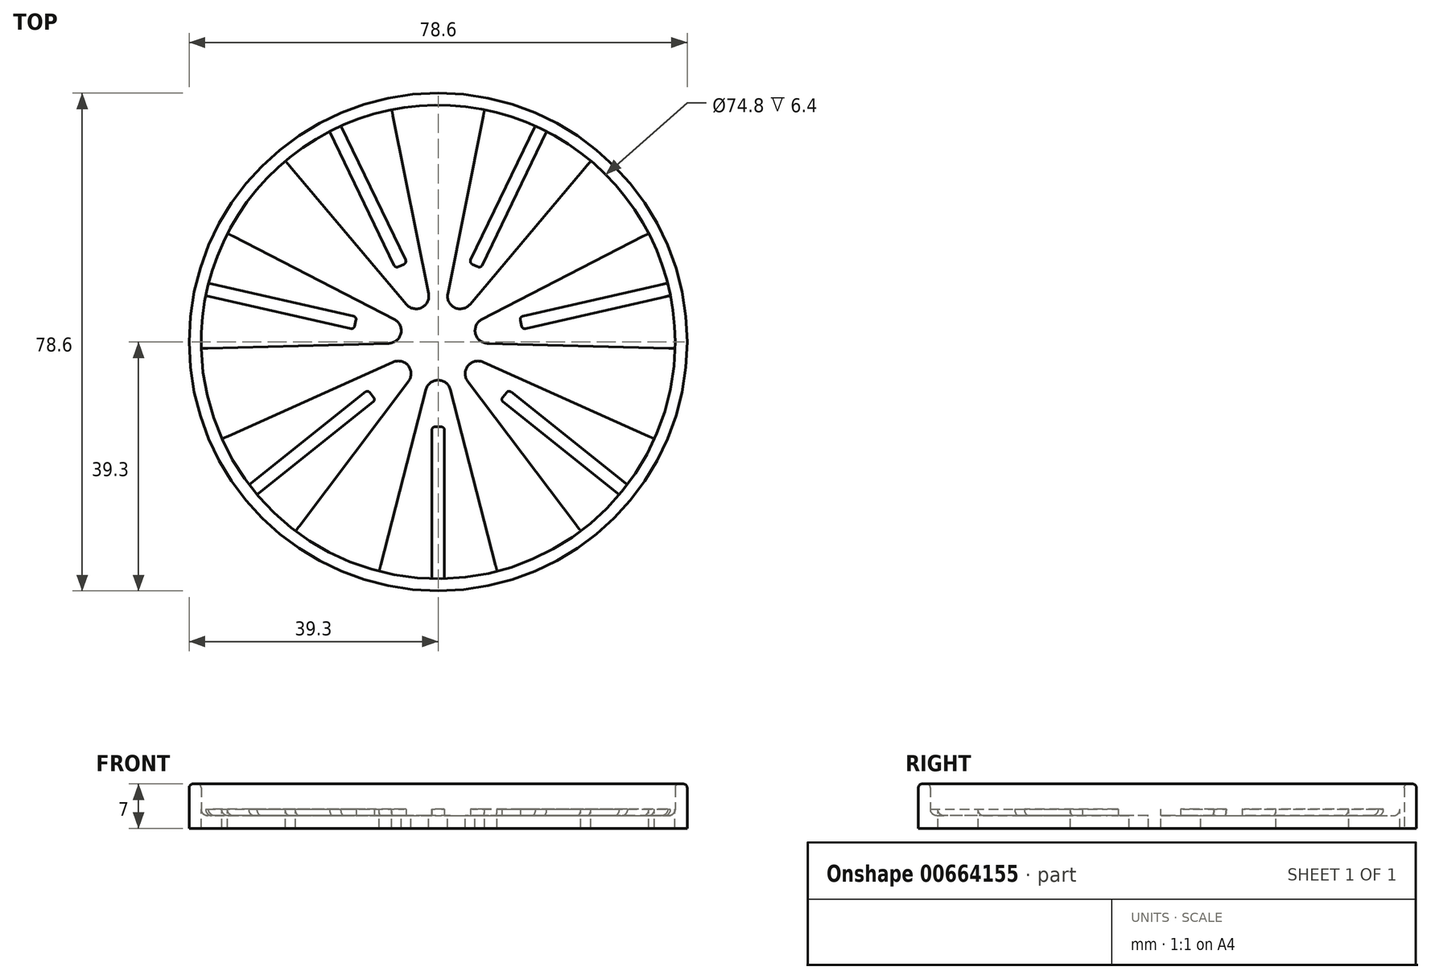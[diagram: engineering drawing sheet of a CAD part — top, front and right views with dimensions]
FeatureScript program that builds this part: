
annotation { "Feature Type Name" : "Feature", "Feature Type Description" : "" }
export const myFeature = defineFeature(function(context is Context, id is Id, definition is map)
    precondition{}
    {
        {
            var Q0;
            Q0=qCreatedBy(makeId("Top.planeOp"),FACE);
            var sketch = newSketch(context, id + "F0", { "sketchPlane" : qUnion([Q0])});
            skCircle(sketch, "E0", {"center": v(0, 0) * mm, "radius": 37.4 * mm});
            skCircle(sketch, "E1", {"center": v(0, 0) * mm, "radius": 39.3 * mm});
            skSolve(sketch);
        }
        {
            var Q0;
            Q0=makeQuery(id+"F0.imprint","IMPRINT",FACE,{"disambiguationData":[TD([[makeQuery(id+"F0.imprint","IMPRINT",EDGE,{"derivedFrom":sQuery(id+"F0.wireOp",EDGE,"E0")}),-1.0]])]});
            extrude(context, id + "F1", {"entities" : qUnion([Q0]), "depth" : 7 * mm, "offsetDistance" : 25 * mm});
        }
        {
            var Q0;
            Q0=qCreatedBy(makeId("Top.planeOp"),FACE);
            var sketch = newSketch(context, id + "F2", { "sketchPlane" : qUnion([Q0])});
            skCircle(sketch, "E2", {"center": v(0, 0) * mm, "radius": 37.45 * mm});
            skSolve(sketch);
        }
        {
            var Q0;
            Q0=makeQuery(id+"F2.imprint","IMPRINT",FACE,{"disambiguationData":[TD([[makeQuery(id+"F2.imprint","IMPRINT",EDGE,{"derivedFrom":sQuery(id+"F2.wireOp",EDGE,"E2")}),1.0]])]});
            extrude(context, id + "F3", {"entities" : qUnion([Q0]), "operationType" : NewBodyOperationType.ADD, "depth" : 2 * mm, "offsetDistance" : 25 * mm});
        }
        {
            var Q0;
            Q0=makeQuery(id+"F3.opExtrude","CAP_FACE",FACE,{"disambiguationData":[OSD([sQuery(id+"F2.wireOp",EDGE,"E2")])],"isStart":false});
            var sketch = newSketch(context, id + "F4", { "sketchPlane" : qUnion([Q0])});
            skCircle(sketch, "E3", {"center": v(0, 0) * mm, "radius": 38.06 * mm});
            skLineSegment(sketch, "E4", {"start": v(1.94, -7.53) * mm, "end": v(9.48, -36.86) * mm});
            skLineSegment(sketch, "E5.MirrorCS", {"start": v(-1.94, -7.53) * mm, "end": v(-9.48, -36.86) * mm});
            skPoint(sketch, "E6.orphan", {"position": v(-11.58, -45.02) * mm});
            skPoint(sketch, "E7.orphan", {"position": v(11.58, -45.02) * mm});
            skArc(sketch, "E8.filletArc", {"start": v(1.94, -7.53) * mm, "mid": v(0, -6.03) * mm, "end": v(-1.94, -7.53) * mm});
            skLineSegment(sketch, "E9.1.0", {"start": v(4.68, -6.21) * mm, "end": v(22.91, -30.4) * mm});
            skLineSegment(sketch, "E9.1.1", {"start": v(7.1, -3.18) * mm, "end": v(34.73, -15.57) * mm});
            skArc(sketch, "E9.1.2", {"start": v(7.1, -3.18) * mm, "mid": v(4.71, -3.76) * mm, "end": v(4.68, -6.21) * mm});
            skLineSegment(sketch, "E9.2.0", {"start": v(7.77, -0.21) * mm, "end": v(38.05, -1.04) * mm});
            skLineSegment(sketch, "E9.2.1", {"start": v(6.91, 3.56) * mm, "end": v(33.83, 17.45) * mm});
            skArc(sketch, "E9.2.2", {"start": v(6.91, 3.56) * mm, "mid": v(5.88, 1.34) * mm, "end": v(7.77, -0.21) * mm});
            skLineSegment(sketch, "E9.3.0", {"start": v(5.01, 5.95) * mm, "end": v(24.54, 29.1) * mm});
            skLineSegment(sketch, "E9.3.1", {"start": v(1.52, 7.63) * mm, "end": v(7.45, 37.33) * mm});
            skArc(sketch, "E9.3.2", {"start": v(1.52, 7.63) * mm, "mid": v(2.62, 5.43) * mm, "end": v(5.01, 5.95) * mm});
            skLineSegment(sketch, "E9.4.0", {"start": v(-1.52, 7.63) * mm, "end": v(-7.45, 37.33) * mm});
            skLineSegment(sketch, "E9.4.1", {"start": v(-5.01, 5.95) * mm, "end": v(-24.54, 29.1) * mm});
            skArc(sketch, "E9.4.2", {"start": v(-5.01, 5.95) * mm, "mid": v(-2.62, 5.43) * mm, "end": v(-1.52, 7.63) * mm});
            skLineSegment(sketch, "E9.5.0", {"start": v(-6.91, 3.56) * mm, "end": v(-33.83, 17.45) * mm});
            skLineSegment(sketch, "E9.5.1", {"start": v(-7.77, -0.21) * mm, "end": v(-38.05, -1.04) * mm});
            skArc(sketch, "E9.5.2", {"start": v(-7.77, -0.21) * mm, "mid": v(-5.88, 1.34) * mm, "end": v(-6.91, 3.56) * mm});
            skLineSegment(sketch, "E10.2.6.0", {"start": v(-7.1, -3.18) * mm, "end": v(-34.73, -15.57) * mm});
            skLineSegment(sketch, "E10.3.6.0", {"start": v(-4.68, -6.21) * mm, "end": v(-22.91, -30.4) * mm});
            skArc(sketch, "E10.6.6.0", {"start": v(-4.68, -6.21) * mm, "mid": v(-4.71, -3.76) * mm, "end": v(-7.1, -3.18) * mm});
            skSolve(sketch);
        }
        {
            var Q0;
            {var subQ24=sQuery(id+"F4.wireOp",EDGE,"E8.filletArc");Q0=makeQuery(id+"F4.imprint","IMPRINT",FACE,{"disambiguationData":[TD([[makeQuery(id+"F4.imprint","IMPRINT",EDGE,{"derivedFrom":subQ24}),-1.0]])]});}
            extrude(context, id + "F5", {"entities" : qUnion([Q0]), "operationType" : NewBodyOperationType.REMOVE, "oppositeDirection" : true, "depth" : 25 * mm, "offsetDistance" : 25 * mm});
        }
        {
            var Q0;
            Q0=makeQuery(id+"F3.boolean.opBoolean","MERGE",FACE,{"derivedFrom":[makeQuery(id+"F1.opExtrude","CAP_FACE",FACE,{"disambiguationData":[OSD([sQuery(id+"F0.wireOp",EDGE,"E0"),sQuery(id+"F0.wireOp",EDGE,"E1")])],"isStart":true}),makeQuery(id+"F3.opExtrude","CAP_FACE",FACE,{"disambiguationData":[OSD([sQuery(id+"F2.wireOp",EDGE,"E2")])],"isStart":true})]});
            var sketch = newSketch(context, id + "F6", { "sketchPlane" : qUnion([Q0])});
            skLineSegment(sketch, "E11", {"start": v(1, 38.32) * mm, "end": v(1, 13.9) * mm});
            skLineSegment(sketch, "E12", {"start": v(0.5, 13.4) * mm, "end": v(-0.5, 13.4) * mm});
            skLineSegment(sketch, "E13", {"start": v(-1, 13.9) * mm, "end": v(-1, 38.32) * mm});
            skPoint(sketch, "E14.visualSharp", {"position": v(-1, 13.4) * mm});
            skArc(sketch, "E14.filletArc", {"start": v(-1, 13.9) * mm, "mid": v(-0.85, 13.55) * mm, "end": v(-0.5, 13.4) * mm});
            skPoint(sketch, "E15.visualSharp", {"position": v(1, 13.4) * mm});
            skArc(sketch, "E15.filletArc", {"start": v(0.5, 13.4) * mm, "mid": v(0.85, 13.55) * mm, "end": v(1, 13.9) * mm});
            skLineSegment(sketch, "E16", {"start": v(-0.5, 38.82) * mm, "end": v(0.5, 38.82) * mm});
            skPoint(sketch, "E17.visualSharp", {"position": v(-1, 38.82) * mm});
            skArc(sketch, "E17.filletArc", {"start": v(-0.5, 38.82) * mm, "mid": v(-0.85, 38.68) * mm, "end": v(-1, 38.32) * mm});
            skPoint(sketch, "E18.visualSharp", {"position": v(1, 38.82) * mm});
            skArc(sketch, "E18.filletArc", {"start": v(1, 38.32) * mm, "mid": v(0.85, 38.68) * mm, "end": v(0.5, 38.82) * mm});
            skPoint(sketch, "E19.1.0", {"position": v(-11.1, 7.58) * mm});
            skPoint(sketch, "E19.1.1", {"position": v(-29.73, 24.99) * mm});
            skLineSegment(sketch, "E19.1.2", {"start": v(-11.5, 7.89) * mm, "end": v(-30.59, 23.11) * mm});
            skPoint(sketch, "E19.1.3", {"position": v(-30.98, 23.42) * mm});
            skLineSegment(sketch, "E19.1.4", {"start": v(-29.34, 24.68) * mm, "end": v(-10.25, 9.45) * mm});
            skPoint(sketch, "E19.1.5", {"position": v(-9.86, 9.14) * mm});
            skArc(sketch, "E19.1.6", {"start": v(-10.17, 8.75) * mm, "mid": v(-10.07, 9.12) * mm, "end": v(-10.25, 9.45) * mm});
            skArc(sketch, "E19.1.7", {"start": v(-30.66, 23.81) * mm, "mid": v(-30.77, 23.45) * mm, "end": v(-30.59, 23.11) * mm});
            skArc(sketch, "E19.1.8", {"start": v(-11.5, 7.89) * mm, "mid": v(-11.13, 7.78) * mm, "end": v(-10.8, 7.97) * mm});
            skLineSegment(sketch, "E19.1.9", {"start": v(-10.17, 8.75) * mm, "end": v(-10.8, 7.97) * mm});
            skLineSegment(sketch, "E19.1.10", {"start": v(-30.66, 23.81) * mm, "end": v(-30.04, 24.6) * mm});
            skArc(sketch, "E19.1.11", {"start": v(-29.34, 24.68) * mm, "mid": v(-29.7, 24.78) * mm, "end": v(-30.04, 24.6) * mm});
            skPoint(sketch, "E19.2.0", {"position": v(-12.85, -3.96) * mm});
            skPoint(sketch, "E19.2.1", {"position": v(-38.07, -7.66) * mm});
            skLineSegment(sketch, "E19.2.2", {"start": v(-13.34, -4.07) * mm, "end": v(-37.14, -9.5) * mm});
            skPoint(sketch, "E19.2.3", {"position": v(-37.63, -9.61) * mm});
            skLineSegment(sketch, "E19.2.4", {"start": v(-37.58, -7.55) * mm, "end": v(-13.78, -2.12) * mm});
            skPoint(sketch, "E19.2.5", {"position": v(-13.3, -2) * mm});
            skArc(sketch, "E19.2.6", {"start": v(-13.18, -2.5) * mm, "mid": v(-13.4, -2.18) * mm, "end": v(-13.78, -2.12) * mm});
            skArc(sketch, "E19.2.7", {"start": v(-37.74, -9.13) * mm, "mid": v(-37.52, -9.44) * mm, "end": v(-37.14, -9.5) * mm});
            skArc(sketch, "E19.2.8", {"start": v(-13.34, -4.07) * mm, "mid": v(-13.03, -3.85) * mm, "end": v(-12.96, -3.47) * mm});
            skLineSegment(sketch, "E19.2.9", {"start": v(-13.18, -2.5) * mm, "end": v(-12.96, -3.47) * mm});
            skLineSegment(sketch, "E19.2.10", {"start": v(-37.74, -9.13) * mm, "end": v(-37.96, -8.15) * mm});
            skArc(sketch, "E19.2.11", {"start": v(-37.58, -7.55) * mm, "mid": v(-37.9, -7.77) * mm, "end": v(-37.96, -8.15) * mm});
            skPoint(sketch, "E19.3.0", {"position": v(-4.92, -12.51) * mm});
            skPoint(sketch, "E19.3.1", {"position": v(-17.75, -34.54) * mm});
            skLineSegment(sketch, "E19.3.2", {"start": v(-5.13, -12.96) * mm, "end": v(-15.73, -34.96) * mm});
            skPoint(sketch, "E19.3.3", {"position": v(-15.94, -35.41) * mm});
            skLineSegment(sketch, "E19.3.4", {"start": v(-17.53, -34.1) * mm, "end": v(-6.94, -12.1) * mm});
            skPoint(sketch, "E19.3.5", {"position": v(-6.72, -11.65) * mm});
            skArc(sketch, "E19.3.6", {"start": v(-6.27, -11.86) * mm, "mid": v(-6.65, -11.84) * mm, "end": v(-6.94, -12.1) * mm});
            skArc(sketch, "E19.3.7", {"start": v(-16.4, -35.2) * mm, "mid": v(-16.01, -35.22) * mm, "end": v(-15.73, -34.96) * mm});
            skArc(sketch, "E19.3.8", {"start": v(-5.13, -12.96) * mm, "mid": v(-5.11, -12.58) * mm, "end": v(-5.37, -12.3) * mm});
            skLineSegment(sketch, "E19.3.9", {"start": v(-6.27, -11.86) * mm, "end": v(-5.37, -12.3) * mm});
            skLineSegment(sketch, "E19.3.10", {"start": v(-16.4, -35.2) * mm, "end": v(-17.3, -34.76) * mm});
            skArc(sketch, "E19.3.11", {"start": v(-17.53, -34.1) * mm, "mid": v(-17.55, -34.48) * mm, "end": v(-17.3, -34.76) * mm});
            skPoint(sketch, "E19.4.0", {"position": v(6.72, -11.65) * mm});
            skPoint(sketch, "E19.4.1", {"position": v(15.94, -35.41) * mm});
            skLineSegment(sketch, "E19.4.2", {"start": v(6.94, -12.1) * mm, "end": v(17.53, -34.1) * mm});
            skPoint(sketch, "E19.4.3", {"position": v(17.75, -34.54) * mm});
            skLineSegment(sketch, "E19.4.4", {"start": v(15.73, -34.96) * mm, "end": v(5.13, -12.96) * mm});
            skPoint(sketch, "E19.4.5", {"position": v(4.92, -12.51) * mm});
            skArc(sketch, "E19.4.6", {"start": v(5.37, -12.3) * mm, "mid": v(5.11, -12.58) * mm, "end": v(5.13, -12.96) * mm});
            skArc(sketch, "E19.4.7", {"start": v(17.3, -34.76) * mm, "mid": v(17.55, -34.48) * mm, "end": v(17.53, -34.1) * mm});
            skArc(sketch, "E19.4.8", {"start": v(6.94, -12.1) * mm, "mid": v(6.65, -11.84) * mm, "end": v(6.27, -11.86) * mm});
            skLineSegment(sketch, "E19.4.9", {"start": v(5.37, -12.3) * mm, "end": v(6.27, -11.86) * mm});
            skLineSegment(sketch, "E19.4.10", {"start": v(17.3, -34.76) * mm, "end": v(16.4, -35.2) * mm});
            skArc(sketch, "E19.4.11", {"start": v(15.73, -34.96) * mm, "mid": v(16.01, -35.22) * mm, "end": v(16.4, -35.2) * mm});
            skPoint(sketch, "E19.5.0", {"position": v(13.3, -2) * mm});
            skPoint(sketch, "E19.5.1", {"position": v(37.63, -9.61) * mm});
            skLineSegment(sketch, "E19.5.2", {"start": v(13.78, -2.12) * mm, "end": v(37.58, -7.55) * mm});
            skPoint(sketch, "E19.5.3", {"position": v(38.07, -7.66) * mm});
            skLineSegment(sketch, "E19.5.4", {"start": v(37.14, -9.5) * mm, "end": v(13.34, -4.07) * mm});
            skPoint(sketch, "E19.5.5", {"position": v(12.85, -3.96) * mm});
            skArc(sketch, "E19.5.6", {"start": v(12.96, -3.47) * mm, "mid": v(13.03, -3.85) * mm, "end": v(13.34, -4.07) * mm});
            skArc(sketch, "E19.5.7", {"start": v(37.96, -8.15) * mm, "mid": v(37.9, -7.77) * mm, "end": v(37.58, -7.55) * mm});
            skArc(sketch, "E19.5.8", {"start": v(13.78, -2.12) * mm, "mid": v(13.4, -2.18) * mm, "end": v(13.18, -2.5) * mm});
            skLineSegment(sketch, "E19.5.9", {"start": v(12.96, -3.47) * mm, "end": v(13.18, -2.5) * mm});
            skLineSegment(sketch, "E19.5.10", {"start": v(37.96, -8.15) * mm, "end": v(37.74, -9.13) * mm});
            skArc(sketch, "E19.5.11", {"start": v(37.14, -9.5) * mm, "mid": v(37.52, -9.44) * mm, "end": v(37.74, -9.13) * mm});
            skPoint(sketch, "E19.6.0", {"position": v(9.86, 9.14) * mm});
            skPoint(sketch, "E19.6.1", {"position": v(30.98, 23.42) * mm});
            skLineSegment(sketch, "E19.6.2", {"start": v(10.25, 9.45) * mm, "end": v(29.34, 24.68) * mm});
            skPoint(sketch, "E19.6.3", {"position": v(29.73, 24.99) * mm});
            skLineSegment(sketch, "E19.6.4", {"start": v(30.59, 23.11) * mm, "end": v(11.5, 7.89) * mm});
            skPoint(sketch, "E19.6.5", {"position": v(11.1, 7.58) * mm});
            skArc(sketch, "E19.6.6", {"start": v(10.8, 7.97) * mm, "mid": v(11.13, 7.78) * mm, "end": v(11.5, 7.89) * mm});
            skArc(sketch, "E19.6.7", {"start": v(30.04, 24.6) * mm, "mid": v(29.7, 24.78) * mm, "end": v(29.34, 24.68) * mm});
            skArc(sketch, "E19.6.8", {"start": v(10.25, 9.45) * mm, "mid": v(10.07, 9.12) * mm, "end": v(10.17, 8.75) * mm});
            skLineSegment(sketch, "E19.6.9", {"start": v(10.8, 7.97) * mm, "end": v(10.17, 8.75) * mm});
            skLineSegment(sketch, "E19.6.10", {"start": v(30.04, 24.6) * mm, "end": v(30.66, 23.81) * mm});
            skArc(sketch, "E19.6.11", {"start": v(30.59, 23.11) * mm, "mid": v(30.77, 23.45) * mm, "end": v(30.66, 23.81) * mm});
            skPoint(sketch, "E19.center", {"position": v(0, 0) * mm});
            skSolve(sketch);
        }
        {
            var Q0;
            Q0 = qSketchRegion(id + "F6", true);
            extrude(context, id + "F7", {"entities" : qUnion([Q0]), "operationType" : NewBodyOperationType.ADD, "depth" : -3 * mm, "offsetDistance" : 25 * mm});
        }
        {
            var Q0;
            {var subQ0=sQuery(id+"F2.wireOp",EDGE,"E2");var subQ1=makeQuery(id+"F3.opExtrude","CAP_FACE",FACE,{"disambiguationData":[OSD([subQ0])],"isStart":false});var subQ2=sQuery(id+"F0.wireOp",EDGE,"E0");var subQ3=makeQuery(id+"F1.opExtrude","SWEPT_FACE",FACE,{"disambiguationData":[OSD([subQ2])]});var subQ4=makeQuery(id+"F3.boolean.opBoolean","INTERSECT",EDGE,{"derivedFrom":[subQ3,subQ1]});var subQ5=sQuery(id+"F4.wireOp",EDGE,"E10.2.6.0");var subQ8=makeQuery(id+"F5.opExtrude","SWEPT_FACE",FACE,{"disambiguationData":[OSD([subQ5])]});Q0=makeQuery(id+"F7.boolean.opBoolean","SPLIT",EDGE,{"disambiguationData":[TD([makeQuery(id+"F5.boolean.opBoolean","COPY",FACE,{"derivedFrom":subQ8})])],"derivedFrom":makeQuery(id+"F5.boolean.opBoolean","SPLIT",EDGE,{"disambiguationData":[TD([subQ8])],"derivedFrom":subQ4})});}
            var Q1;
            {var subQ0=sQuery(id+"F2.wireOp",EDGE,"E2");var subQ1=makeQuery(id+"F3.opExtrude","CAP_FACE",FACE,{"disambiguationData":[OSD([subQ0])],"isStart":false});var subQ2=sQuery(id+"F0.wireOp",EDGE,"E0");var subQ3=makeQuery(id+"F1.opExtrude","SWEPT_FACE",FACE,{"disambiguationData":[OSD([subQ2])]});var subQ4=makeQuery(id+"F3.boolean.opBoolean","INTERSECT",EDGE,{"derivedFrom":[subQ3,subQ1]});var subQ6=sQuery(id+"F4.wireOp",EDGE,"E5.MirrorCS");var subQ7=makeQuery(id+"F5.opExtrude","SWEPT_FACE",FACE,{"disambiguationData":[OSD([subQ6])]});var subQ12=sQuery(id+"F4.wireOp",EDGE,"E4");Q1=makeQuery(id+"F7.boolean.opBoolean","SPLIT",EDGE,{"disambiguationData":[TD([makeQuery(id+"F5.boolean.opBoolean","COPY",FACE,{"derivedFrom":subQ7})])],"derivedFrom":makeQuery(id+"F5.boolean.opBoolean","SPLIT",EDGE,{"disambiguationData":[TD([makeQuery(id+"F5.opExtrude","SWEPT_FACE",FACE,{"disambiguationData":[OSD([subQ12])]})])],"derivedFrom":subQ4})});}
            var Q2;
            {var subQ0=sQuery(id+"F2.wireOp",EDGE,"E2");var subQ1=makeQuery(id+"F3.opExtrude","CAP_FACE",FACE,{"disambiguationData":[OSD([subQ0])],"isStart":false});var subQ2=sQuery(id+"F0.wireOp",EDGE,"E0");var subQ3=makeQuery(id+"F1.opExtrude","SWEPT_FACE",FACE,{"disambiguationData":[OSD([subQ2])]});var subQ4=makeQuery(id+"F3.boolean.opBoolean","INTERSECT",EDGE,{"derivedFrom":[subQ3,subQ1]});var subQ9=sQuery(id+"F4.wireOp",EDGE,"E4");var subQ10=makeQuery(id+"F5.opExtrude","SWEPT_FACE",FACE,{"disambiguationData":[OSD([subQ9])]});Q2=makeQuery(id+"F7.boolean.opBoolean","SPLIT",EDGE,{"disambiguationData":[TD([makeQuery(id+"F5.boolean.opBoolean","COPY",FACE,{"derivedFrom":subQ10})])],"derivedFrom":makeQuery(id+"F5.boolean.opBoolean","SPLIT",EDGE,{"disambiguationData":[TD([subQ10])],"derivedFrom":subQ4})});}
            var Q3;
            {var subQ0=sQuery(id+"F2.wireOp",EDGE,"E2");var subQ1=makeQuery(id+"F3.opExtrude","CAP_FACE",FACE,{"disambiguationData":[OSD([subQ0])],"isStart":false});var subQ2=sQuery(id+"F0.wireOp",EDGE,"E0");var subQ3=makeQuery(id+"F1.opExtrude","SWEPT_FACE",FACE,{"disambiguationData":[OSD([subQ2])]});var subQ4=makeQuery(id+"F3.boolean.opBoolean","INTERSECT",EDGE,{"derivedFrom":[subQ3,subQ1]});var subQ5=sQuery(id+"F4.wireOp",EDGE,"E10.2.6.0");var subQ7=sQuery(id+"F4.wireOp",EDGE,"E10.3.6.0");var subQ8=makeQuery(id+"F5.opExtrude","SWEPT_FACE",FACE,{"disambiguationData":[OSD([subQ7])]});Q3=makeQuery(id+"F7.boolean.opBoolean","SPLIT",EDGE,{"disambiguationData":[TD([makeQuery(id+"F5.boolean.opBoolean","COPY",FACE,{"derivedFrom":subQ8})])],"derivedFrom":makeQuery(id+"F5.boolean.opBoolean","SPLIT",EDGE,{"disambiguationData":[TD([makeQuery(id+"F5.opExtrude","SWEPT_FACE",FACE,{"disambiguationData":[OSD([subQ5])]})])],"derivedFrom":subQ4})});}
            var Q4;
            {var subQ0=sQuery(id+"F2.wireOp",EDGE,"E2");var subQ1=makeQuery(id+"F3.opExtrude","CAP_FACE",FACE,{"disambiguationData":[OSD([subQ0])],"isStart":false});var subQ2=sQuery(id+"F0.wireOp",EDGE,"E0");var subQ3=makeQuery(id+"F1.opExtrude","SWEPT_FACE",FACE,{"disambiguationData":[OSD([subQ2])]});var subQ4=makeQuery(id+"F3.boolean.opBoolean","INTERSECT",EDGE,{"derivedFrom":[subQ3,subQ1]});var subQ11=sQuery(id+"F4.wireOp",EDGE,"E9.1.0");var subQ12=makeQuery(id+"F5.opExtrude","SWEPT_FACE",FACE,{"disambiguationData":[OSD([subQ11])]});Q4=makeQuery(id+"F7.boolean.opBoolean","SPLIT",EDGE,{"disambiguationData":[TD([makeQuery(id+"F5.boolean.opBoolean","COPY",FACE,{"derivedFrom":subQ12})])],"derivedFrom":makeQuery(id+"F5.boolean.opBoolean","SPLIT",EDGE,{"disambiguationData":[TD([subQ12])],"derivedFrom":subQ4})});}
            var Q5;
            {var subQ0=sQuery(id+"F4.wireOp",EDGE,"E9.1.1");var subQ1=makeQuery(id+"F5.opExtrude","SWEPT_FACE",FACE,{"disambiguationData":[OSD([subQ0])]});var subQ2=sQuery(id+"F2.wireOp",EDGE,"E2");var subQ3=makeQuery(id+"F3.opExtrude","CAP_FACE",FACE,{"disambiguationData":[OSD([subQ2])],"isStart":false});var subQ4=sQuery(id+"F0.wireOp",EDGE,"E0");var subQ5=makeQuery(id+"F1.opExtrude","SWEPT_FACE",FACE,{"disambiguationData":[OSD([subQ4])]});var subQ6=makeQuery(id+"F3.boolean.opBoolean","INTERSECT",EDGE,{"derivedFrom":[subQ5,subQ3]});var subQ12=sQuery(id+"F4.wireOp",EDGE,"E9.1.0");Q5=makeQuery(id+"F7.boolean.opBoolean","SPLIT",EDGE,{"disambiguationData":[TD([makeQuery(id+"F5.boolean.opBoolean","COPY",FACE,{"derivedFrom":subQ1})])],"derivedFrom":makeQuery(id+"F5.boolean.opBoolean","SPLIT",EDGE,{"disambiguationData":[TD([makeQuery(id+"F5.opExtrude","SWEPT_FACE",FACE,{"disambiguationData":[OSD([subQ12])]})])],"derivedFrom":subQ6})});}
            var Q6;
            {var subQ0=sQuery(id+"F4.wireOp",EDGE,"E9.5.0");var subQ1=makeQuery(id+"F5.opExtrude","SWEPT_FACE",FACE,{"disambiguationData":[OSD([subQ0])]});var subQ2=sQuery(id+"F2.wireOp",EDGE,"E2");var subQ3=makeQuery(id+"F3.opExtrude","CAP_FACE",FACE,{"disambiguationData":[OSD([subQ2])],"isStart":false});var subQ4=sQuery(id+"F0.wireOp",EDGE,"E0");var subQ5=makeQuery(id+"F1.opExtrude","SWEPT_FACE",FACE,{"disambiguationData":[OSD([subQ4])]});var subQ6=makeQuery(id+"F3.boolean.opBoolean","INTERSECT",EDGE,{"derivedFrom":[subQ5,subQ3]});Q6=makeQuery(id+"F7.boolean.opBoolean","SPLIT",EDGE,{"disambiguationData":[TD([makeQuery(id+"F5.boolean.opBoolean","COPY",FACE,{"derivedFrom":subQ1})])],"derivedFrom":makeQuery(id+"F5.boolean.opBoolean","SPLIT",EDGE,{"disambiguationData":[TD([subQ1])],"derivedFrom":subQ6})});}
            var Q7;
            {var subQ0=sQuery(id+"F4.wireOp",EDGE,"E9.4.1");var subQ1=makeQuery(id+"F5.opExtrude","SWEPT_FACE",FACE,{"disambiguationData":[OSD([subQ0])]});var subQ2=sQuery(id+"F2.wireOp",EDGE,"E2");var subQ3=makeQuery(id+"F3.opExtrude","CAP_FACE",FACE,{"disambiguationData":[OSD([subQ2])],"isStart":false});var subQ4=sQuery(id+"F0.wireOp",EDGE,"E0");var subQ5=makeQuery(id+"F1.opExtrude","SWEPT_FACE",FACE,{"disambiguationData":[OSD([subQ4])]});var subQ6=makeQuery(id+"F3.boolean.opBoolean","INTERSECT",EDGE,{"derivedFrom":[subQ5,subQ3]});var subQ12=sQuery(id+"F4.wireOp",EDGE,"E9.4.0");Q7=makeQuery(id+"F7.boolean.opBoolean","SPLIT",EDGE,{"disambiguationData":[TD([makeQuery(id+"F5.boolean.opBoolean","COPY",FACE,{"derivedFrom":subQ1})])],"derivedFrom":makeQuery(id+"F5.boolean.opBoolean","SPLIT",EDGE,{"disambiguationData":[TD([makeQuery(id+"F5.opExtrude","SWEPT_FACE",FACE,{"disambiguationData":[OSD([subQ12])]})])],"derivedFrom":subQ6})});}
            var Q8;
            {var subQ0=sQuery(id+"F2.wireOp",EDGE,"E2");var subQ1=makeQuery(id+"F3.opExtrude","CAP_FACE",FACE,{"disambiguationData":[OSD([subQ0])],"isStart":false});var subQ2=sQuery(id+"F0.wireOp",EDGE,"E0");var subQ3=makeQuery(id+"F1.opExtrude","SWEPT_FACE",FACE,{"disambiguationData":[OSD([subQ2])]});var subQ4=makeQuery(id+"F3.boolean.opBoolean","INTERSECT",EDGE,{"derivedFrom":[subQ3,subQ1]});var subQ6=sQuery(id+"F4.wireOp",EDGE,"E9.4.0");var subQ7=makeQuery(id+"F5.opExtrude","SWEPT_FACE",FACE,{"disambiguationData":[OSD([subQ6])]});Q8=makeQuery(id+"F7.boolean.opBoolean","SPLIT",EDGE,{"disambiguationData":[TD([makeQuery(id+"F5.boolean.opBoolean","COPY",FACE,{"derivedFrom":subQ7})])],"derivedFrom":makeQuery(id+"F5.boolean.opBoolean","SPLIT",EDGE,{"disambiguationData":[TD([subQ7])],"derivedFrom":subQ4})});}
            var Q9;
            {var subQ0=sQuery(id+"F4.wireOp",EDGE,"E9.5.1");var subQ1=makeQuery(id+"F5.opExtrude","SWEPT_FACE",FACE,{"disambiguationData":[OSD([subQ0])]});var subQ2=sQuery(id+"F2.wireOp",EDGE,"E2");var subQ3=makeQuery(id+"F3.opExtrude","CAP_FACE",FACE,{"disambiguationData":[OSD([subQ2])],"isStart":false});var subQ4=sQuery(id+"F0.wireOp",EDGE,"E0");var subQ5=makeQuery(id+"F1.opExtrude","SWEPT_FACE",FACE,{"disambiguationData":[OSD([subQ4])]});var subQ6=makeQuery(id+"F3.boolean.opBoolean","INTERSECT",EDGE,{"derivedFrom":[subQ5,subQ3]});var subQ9=sQuery(id+"F4.wireOp",EDGE,"E9.5.0");Q9=makeQuery(id+"F7.boolean.opBoolean","SPLIT",EDGE,{"disambiguationData":[TD([makeQuery(id+"F5.boolean.opBoolean","COPY",FACE,{"derivedFrom":subQ1})])],"derivedFrom":makeQuery(id+"F5.boolean.opBoolean","SPLIT",EDGE,{"disambiguationData":[TD([makeQuery(id+"F5.opExtrude","SWEPT_FACE",FACE,{"disambiguationData":[OSD([subQ9])]})])],"derivedFrom":subQ6})});}
            var Q10;
            {var subQ0=sQuery(id+"F4.wireOp",EDGE,"E9.2.0");var subQ1=makeQuery(id+"F5.opExtrude","SWEPT_FACE",FACE,{"disambiguationData":[OSD([subQ0])]});var subQ2=sQuery(id+"F2.wireOp",EDGE,"E2");var subQ3=makeQuery(id+"F3.opExtrude","CAP_FACE",FACE,{"disambiguationData":[OSD([subQ2])],"isStart":false});var subQ4=sQuery(id+"F0.wireOp",EDGE,"E0");var subQ5=makeQuery(id+"F1.opExtrude","SWEPT_FACE",FACE,{"disambiguationData":[OSD([subQ4])]});var subQ6=makeQuery(id+"F3.boolean.opBoolean","INTERSECT",EDGE,{"derivedFrom":[subQ5,subQ3]});Q10=makeQuery(id+"F7.boolean.opBoolean","SPLIT",EDGE,{"disambiguationData":[TD([makeQuery(id+"F5.boolean.opBoolean","COPY",FACE,{"derivedFrom":subQ1})])],"derivedFrom":makeQuery(id+"F5.boolean.opBoolean","SPLIT",EDGE,{"disambiguationData":[TD([subQ1])],"derivedFrom":subQ6})});}
            var Q11;
            {var subQ0=sQuery(id+"F2.wireOp",EDGE,"E2");var subQ1=makeQuery(id+"F3.opExtrude","CAP_FACE",FACE,{"disambiguationData":[OSD([subQ0])],"isStart":false});var subQ2=sQuery(id+"F0.wireOp",EDGE,"E0");var subQ3=makeQuery(id+"F1.opExtrude","SWEPT_FACE",FACE,{"disambiguationData":[OSD([subQ2])]});var subQ4=makeQuery(id+"F3.boolean.opBoolean","INTERSECT",EDGE,{"derivedFrom":[subQ3,subQ1]});var subQ7=sQuery(id+"F4.wireOp",EDGE,"E9.2.1");var subQ9=sQuery(id+"F4.wireOp",EDGE,"E9.2.0");var subQ12=makeQuery(id+"F5.opExtrude","SWEPT_FACE",FACE,{"disambiguationData":[OSD([subQ7])]});Q11=makeQuery(id+"F7.boolean.opBoolean","SPLIT",EDGE,{"disambiguationData":[TD([makeQuery(id+"F5.boolean.opBoolean","COPY",FACE,{"derivedFrom":subQ12})])],"derivedFrom":makeQuery(id+"F5.boolean.opBoolean","SPLIT",EDGE,{"disambiguationData":[TD([makeQuery(id+"F5.opExtrude","SWEPT_FACE",FACE,{"disambiguationData":[OSD([subQ9])]})])],"derivedFrom":subQ4})});}
            var Q12;
            {var subQ0=sQuery(id+"F2.wireOp",EDGE,"E2");var subQ1=makeQuery(id+"F3.opExtrude","CAP_FACE",FACE,{"disambiguationData":[OSD([subQ0])],"isStart":false});var subQ2=sQuery(id+"F0.wireOp",EDGE,"E0");var subQ3=makeQuery(id+"F1.opExtrude","SWEPT_FACE",FACE,{"disambiguationData":[OSD([subQ2])]});var subQ4=makeQuery(id+"F3.boolean.opBoolean","INTERSECT",EDGE,{"derivedFrom":[subQ3,subQ1]});var subQ7=sQuery(id+"F4.wireOp",EDGE,"E9.3.0");var subQ9=makeQuery(id+"F5.opExtrude","SWEPT_FACE",FACE,{"disambiguationData":[OSD([subQ7])]});Q12=makeQuery(id+"F7.boolean.opBoolean","SPLIT",EDGE,{"disambiguationData":[TD([makeQuery(id+"F5.boolean.opBoolean","COPY",FACE,{"derivedFrom":subQ9})])],"derivedFrom":makeQuery(id+"F5.boolean.opBoolean","SPLIT",EDGE,{"disambiguationData":[TD([subQ9])],"derivedFrom":subQ4})});}
            var Q13;
            {var subQ0=sQuery(id+"F2.wireOp",EDGE,"E2");var subQ1=makeQuery(id+"F3.opExtrude","CAP_FACE",FACE,{"disambiguationData":[OSD([subQ0])],"isStart":false});var subQ2=sQuery(id+"F0.wireOp",EDGE,"E0");var subQ3=makeQuery(id+"F1.opExtrude","SWEPT_FACE",FACE,{"disambiguationData":[OSD([subQ2])]});var subQ4=makeQuery(id+"F3.boolean.opBoolean","INTERSECT",EDGE,{"derivedFrom":[subQ3,subQ1]});var subQ7=sQuery(id+"F4.wireOp",EDGE,"E9.3.1");var subQ8=makeQuery(id+"F5.opExtrude","SWEPT_FACE",FACE,{"disambiguationData":[OSD([subQ7])]});var subQ9=sQuery(id+"F4.wireOp",EDGE,"E9.3.0");Q13=makeQuery(id+"F7.boolean.opBoolean","SPLIT",EDGE,{"disambiguationData":[TD([makeQuery(id+"F5.boolean.opBoolean","COPY",FACE,{"derivedFrom":subQ8})])],"derivedFrom":makeQuery(id+"F5.boolean.opBoolean","SPLIT",EDGE,{"disambiguationData":[TD([makeQuery(id+"F5.opExtrude","SWEPT_FACE",FACE,{"disambiguationData":[OSD([subQ9])]})])],"derivedFrom":subQ4})});}
            fillet(context, id + "F8", {"entities" : qUnion([Q0, Q1, Q2, Q3, Q4, Q5, Q6, Q7, Q8, Q9, Q10, Q11, Q12, Q13]), "radius" : 1 * mm, "tangentPropagation" : true, "allowEdgeOverflow" : false});
        }
        {
            var Q0;
            Q0=makeQuery(id+"F1.opExtrude","CAP_EDGE",EDGE,{"disambiguationData":[OSD([sQuery(id+"F0.wireOp",EDGE,"E1")])],"isStart":false});
            var Q1;
            Q1=makeQuery(id+"F1.opExtrude","CAP_EDGE",EDGE,{"disambiguationData":[OSD([sQuery(id+"F0.wireOp",EDGE,"E0")])],"isStart":false});
            fillet(context, id + "F9", {"entities" : qUnion([Q0, Q1]), "radius" : 0.6 * mm, "tangentPropagation" : true, "allowEdgeOverflow" : false});
        }
    });
